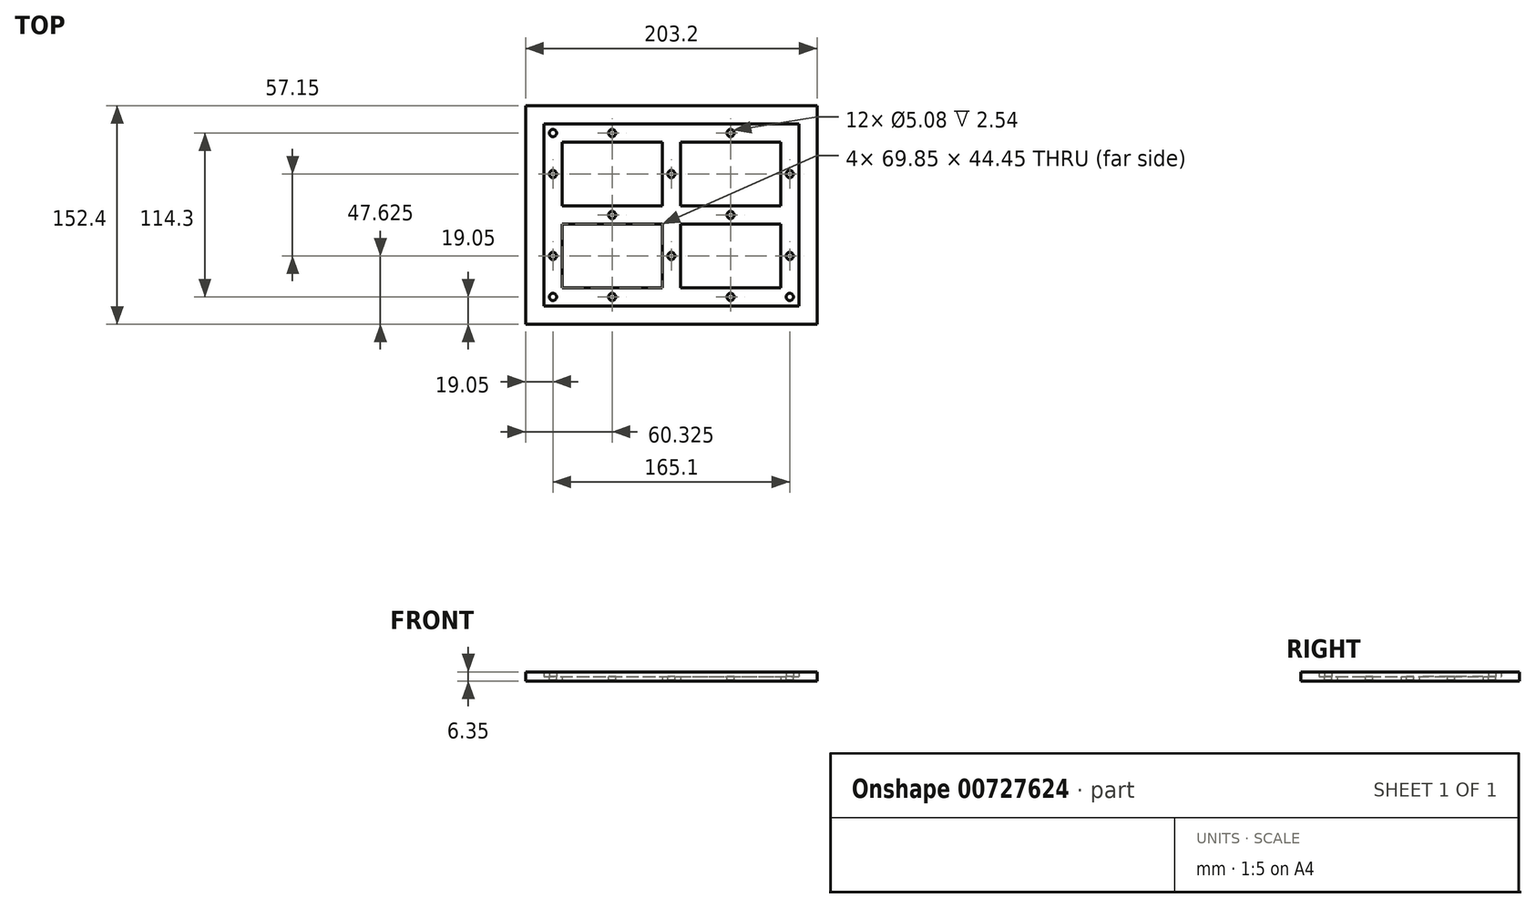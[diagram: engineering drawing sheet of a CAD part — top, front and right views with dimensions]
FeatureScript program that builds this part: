
annotation { "Feature Type Name" : "Feature", "Feature Type Description" : "" }
export const myFeature = defineFeature(function(context is Context, id is Id, definition is map)
    precondition{}
    {
        {
            var Q0;
            Q0=qCreatedBy(makeId("Top.planeOp"),FACE);
            var sketch = newSketch(context, id + "F0", { "sketchPlane" : qUnion([Q0])});
            skLineSegment(sketch, "E0.bottom", {"start": v(0, 0) * mm, "end": v(203.2, 0) * mm});
            skLineSegment(sketch, "E0.top", {"start": v(0, 152.4) * mm, "end": v(203.2, 152.4) * mm});
            skLineSegment(sketch, "E0.left", {"start": v(0, 0) * mm, "end": v(0, 152.4) * mm});
            skLineSegment(sketch, "E0.right", {"start": v(203.2, 0) * mm, "end": v(203.2, 152.4) * mm});
            skLineSegment(sketch, "E1.bottom", {"start": v(12.7, 139.7) * mm, "end": v(190.5, 139.7) * mm});
            skLineSegment(sketch, "E1.top", {"start": v(12.7, 12.7) * mm, "end": v(190.5, 12.7) * mm});
            skLineSegment(sketch, "E1.left", {"start": v(12.7, 139.7) * mm, "end": v(12.7, 12.7) * mm});
            skLineSegment(sketch, "E1.right", {"start": v(190.5, 139.7) * mm, "end": v(190.5, 12.7) * mm});
            skSolve(sketch);
        }
        {
            var Q0;
            Q0 = qSketchRegion(id + "F0", true);
            extrude(context, id + "F1", {"entities" : qUnion([Q0]), "depth" : 6.35 * mm, "offsetDistance" : 25.4 * mm});
        }
        {
            var Q0;
            Q0=qCreatedBy(makeId("Top.planeOp"),FACE);
            var sketch = newSketch(context, id + "F2", { "sketchPlane" : qUnion([Q0])});
            skLineSegment(sketch, "E2.bottom", {"start": v(12.7, 12.7) * mm, "end": v(190.5, 12.7) * mm});
            skLineSegment(sketch, "E2.top", {"start": v(12.7, 139.7) * mm, "end": v(190.5, 139.7) * mm});
            skLineSegment(sketch, "E2.left", {"start": v(12.7, 12.7) * mm, "end": v(12.7, 139.7) * mm});
            skLineSegment(sketch, "E2.right", {"start": v(190.5, 12.7) * mm, "end": v(190.5, 139.7) * mm});
            skLineSegment(sketch, "E3.bottom", {"start": v(25.4, 127) * mm, "end": v(95.25, 127) * mm});
            skLineSegment(sketch, "E3.top", {"start": v(25.4, 82.55) * mm, "end": v(95.25, 82.55) * mm});
            skLineSegment(sketch, "E3.left", {"start": v(25.4, 127) * mm, "end": v(25.4, 82.55) * mm});
            skLineSegment(sketch, "E3.right", {"start": v(95.25, 127) * mm, "end": v(95.25, 82.55) * mm});
            skLineSegment(sketch, "E4.bottom", {"start": v(107.95, 127) * mm, "end": v(177.8, 127) * mm});
            skLineSegment(sketch, "E4.top", {"start": v(107.95, 82.55) * mm, "end": v(177.8, 82.55) * mm});
            skLineSegment(sketch, "E4.left", {"start": v(107.95, 127) * mm, "end": v(107.95, 82.55) * mm});
            skLineSegment(sketch, "E4.right", {"start": v(177.8, 127) * mm, "end": v(177.8, 82.55) * mm});
            skLineSegment(sketch, "E5.bottom", {"start": v(25.4, 25.4) * mm, "end": v(95.25, 25.4) * mm});
            skLineSegment(sketch, "E5.top", {"start": v(25.4, 69.85) * mm, "end": v(95.25, 69.85) * mm});
            skLineSegment(sketch, "E5.left", {"start": v(25.4, 25.4) * mm, "end": v(25.4, 69.85) * mm});
            skLineSegment(sketch, "E5.right", {"start": v(95.25, 25.4) * mm, "end": v(95.25, 69.85) * mm});
            skLineSegment(sketch, "E6.bottom", {"start": v(107.95, 25.4) * mm, "end": v(177.8, 25.4) * mm});
            skLineSegment(sketch, "E6.top", {"start": v(107.95, 69.85) * mm, "end": v(177.8, 69.85) * mm});
            skLineSegment(sketch, "E6.left", {"start": v(107.95, 25.4) * mm, "end": v(107.95, 69.85) * mm});
            skLineSegment(sketch, "E6.right", {"start": v(177.8, 25.4) * mm, "end": v(177.8, 69.85) * mm});
            skSolve(sketch);
        }
        {
            var Q0;
            Q0 = qSketchRegion(id + "F2", true);
            extrude(context, id + "F3", {"entities" : qUnion([Q0]), "operationType" : NewBodyOperationType.ADD, "depth" : 3.17 * mm, "offsetDistance" : 25.4 * mm});
        }
        {
            var Q0;
            Q0=makeQuery(id+"F3.opExtrude","CAP_FACE",FACE,{"disambiguationData":[OSD([sQuery(id+"F2.wireOp",EDGE,"E2.bottom"),sQuery(id+"F2.wireOp",EDGE,"E2.top"),sQuery(id+"F2.wireOp",EDGE,"E2.left"),sQuery(id+"F2.wireOp",EDGE,"E2.right"),sQuery(id+"F2.wireOp",EDGE,"E3.bottom"),sQuery(id+"F2.wireOp",EDGE,"E3.top"),sQuery(id+"F2.wireOp",EDGE,"E3.left"),sQuery(id+"F2.wireOp",EDGE,"E3.right"),sQuery(id+"F2.wireOp",EDGE,"E4.bottom"),sQuery(id+"F2.wireOp",EDGE,"E4.top"),sQuery(id+"F2.wireOp",EDGE,"E4.left"),sQuery(id+"F2.wireOp",EDGE,"E4.right"),sQuery(id+"F2.wireOp",EDGE,"E5.bottom"),sQuery(id+"F2.wireOp",EDGE,"E5.top"),sQuery(id+"F2.wireOp",EDGE,"E5.left"),sQuery(id+"F2.wireOp",EDGE,"E5.right"),sQuery(id+"F2.wireOp",EDGE,"E6.bottom"),sQuery(id+"F2.wireOp",EDGE,"E6.top"),sQuery(id+"F2.wireOp",EDGE,"E6.left"),sQuery(id+"F2.wireOp",EDGE,"E6.right")])],"isStart":false});
            var sketch = newSketch(context, id + "F4", { "sketchPlane" : qUnion([Q0])});
            skCircle(sketch, "E7", {"center": v(19.05, 133.35) * mm, "radius": 2.54 * mm});
            skCircle(sketch, "E8", {"center": v(19.05, 19.05) * mm, "radius": 2.54 * mm});
            skCircle(sketch, "E9", {"center": v(184.15, 19.05) * mm, "radius": 2.54 * mm});
            skSolve(sketch);
        }
        {
            var Q0;
            Q0 = qSketchRegion(id + "F4", true);
            var Q1;
            Q1=makeQuery(id+"F1.opExtrude","CAP_FACE",FACE,{"disambiguationData":[OSD([sQuery(id+"F0.wireOp",EDGE,"E0.bottom"),sQuery(id+"F0.wireOp",EDGE,"E0.top"),sQuery(id+"F0.wireOp",EDGE,"E0.left"),sQuery(id+"F0.wireOp",EDGE,"E0.right"),sQuery(id+"F0.wireOp",EDGE,"E1.bottom"),sQuery(id+"F0.wireOp",EDGE,"E1.top"),sQuery(id+"F0.wireOp",EDGE,"E1.left"),sQuery(id+"F0.wireOp",EDGE,"E1.right")])],"isStart":false});
            extrude(context, id + "F5", {"entities" : qUnion([Q0]), "operationType" : NewBodyOperationType.ADD, "endBound" : BoundingType.UP_TO_SURFACE, "depth" : 25.4 * mm, "endBoundEntityFace" : qUnion([Q1]), "offsetDistance" : 25.4 * mm});
        }
        {
            var Q0;
            Q0=makeQuery(id+"F3.opExtrude","CAP_FACE",FACE,{"disambiguationData":[OSD([sQuery(id+"F2.wireOp",EDGE,"E2.bottom"),sQuery(id+"F2.wireOp",EDGE,"E2.top"),sQuery(id+"F2.wireOp",EDGE,"E2.left"),sQuery(id+"F2.wireOp",EDGE,"E2.right"),sQuery(id+"F2.wireOp",EDGE,"E3.bottom"),sQuery(id+"F2.wireOp",EDGE,"E3.top"),sQuery(id+"F2.wireOp",EDGE,"E3.left"),sQuery(id+"F2.wireOp",EDGE,"E3.right"),sQuery(id+"F2.wireOp",EDGE,"E4.bottom"),sQuery(id+"F2.wireOp",EDGE,"E4.top"),sQuery(id+"F2.wireOp",EDGE,"E4.left"),sQuery(id+"F2.wireOp",EDGE,"E4.right"),sQuery(id+"F2.wireOp",EDGE,"E5.bottom"),sQuery(id+"F2.wireOp",EDGE,"E5.top"),sQuery(id+"F2.wireOp",EDGE,"E5.left"),sQuery(id+"F2.wireOp",EDGE,"E5.right"),sQuery(id+"F2.wireOp",EDGE,"E6.bottom"),sQuery(id+"F2.wireOp",EDGE,"E6.top"),sQuery(id+"F2.wireOp",EDGE,"E6.left"),sQuery(id+"F2.wireOp",EDGE,"E6.right")])],"isStart":false});
            var sketch = newSketch(context, id + "F6", { "sketchPlane" : qUnion([Q0])});
            skCircle(sketch, "E10", {"center": v(60.32, 133.35) * mm, "radius": 2.54 * mm});
            skCircle(sketch, "E11", {"center": v(142.88, 133.35) * mm, "radius": 2.54 * mm});
            skCircle(sketch, "E12", {"center": v(101.6, 47.63) * mm, "radius": 2.54 * mm});
            skCircle(sketch, "E13", {"center": v(101.6, 104.78) * mm, "radius": 2.54 * mm});
            skCircle(sketch, "E14", {"center": v(142.88, 76.2) * mm, "radius": 2.54 * mm});
            skCircle(sketch, "E15", {"center": v(60.33, 19.05) * mm, "radius": 2.54 * mm});
            skCircle(sketch, "E16", {"center": v(184.15, 47.63) * mm, "radius": 2.54 * mm});
            skCircle(sketch, "E17", {"center": v(142.88, 19.05) * mm, "radius": 2.54 * mm});
            skCircle(sketch, "E18", {"center": v(19.05, 47.62) * mm, "radius": 2.54 * mm});
            skCircle(sketch, "E19", {"center": v(184.15, 104.78) * mm, "radius": 2.54 * mm});
            skLineSegment(sketch, "E20", {"start": v(60.32, 127) * mm, "end": v(60.32, 139.7) * mm, "construction": true});
            skLineSegment(sketch, "E21", {"start": v(142.88, 127) * mm, "end": v(142.88, 139.7) * mm, "construction": true});
            skLineSegment(sketch, "E22", {"start": v(95.25, 104.78) * mm, "end": v(107.95, 104.78) * mm, "construction": true});
            skLineSegment(sketch, "E23", {"start": v(95.25, 47.63) * mm, "end": v(107.95, 47.63) * mm, "construction": true});
            skLineSegment(sketch, "E24", {"start": v(60.33, 25.4) * mm, "end": v(60.33, 12.7) * mm, "construction": true});
            skLineSegment(sketch, "E25", {"start": v(142.88, 25.4) * mm, "end": v(142.88, 12.7) * mm, "construction": true});
            skLineSegment(sketch, "E26", {"start": v(177.8, 104.78) * mm, "end": v(190.5, 104.78) * mm, "construction": true});
            skLineSegment(sketch, "E27", {"start": v(177.8, 47.63) * mm, "end": v(190.5, 47.63) * mm, "construction": true});
            skLineSegment(sketch, "E28", {"start": v(142.88, 82.55) * mm, "end": v(142.88, 69.85) * mm, "construction": true});
            skLineSegment(sketch, "E29", {"start": v(60.33, 82.55) * mm, "end": v(60.33, 69.85) * mm, "construction": true});
            skLineSegment(sketch, "E30", {"start": v(25.4, 104.78) * mm, "end": v(12.7, 104.78) * mm, "construction": true});
            skLineSegment(sketch, "E31", {"start": v(25.4, 47.62) * mm, "end": v(12.7, 47.62) * mm, "construction": true});
            skCircle(sketch, "E32", {"center": v(60.33, 76.2) * mm, "radius": 2.54 * mm});
            skCircle(sketch, "E33", {"center": v(19.05, 104.78) * mm, "radius": 2.54 * mm});
            skSolve(sketch);
        }
        {
            var Q0;
            Q0 = qSketchRegion(id + "F6", true);
            extrude(context, id + "F7", {"entities" : qUnion([Q0]), "operationType" : NewBodyOperationType.REMOVE, "oppositeDirection" : true, "depth" : 2.54 * mm, "offsetDistance" : 25.4 * mm});
        }
    });
